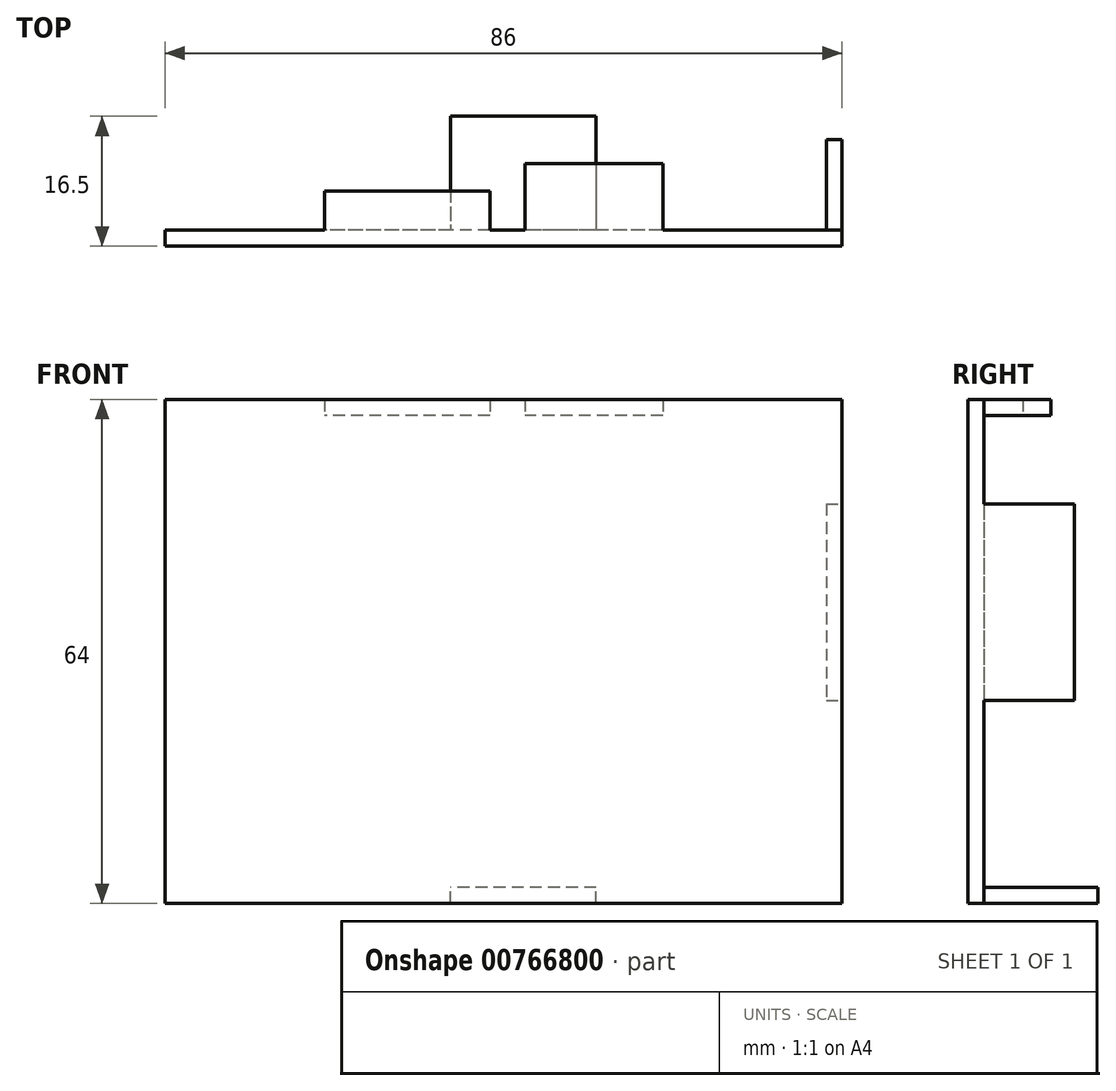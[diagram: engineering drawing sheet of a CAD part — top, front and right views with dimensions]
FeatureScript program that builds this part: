
annotation { "Feature Type Name" : "Feature", "Feature Type Description" : "" }
export const myFeature = defineFeature(function(context is Context, id is Id, definition is map)
    precondition{}
    {
        {
            var Q0;
            Q0=qCreatedBy(makeId("Front.planeOp"),FACE);
            var sketch = newSketch(context, id + "F0", { "sketchPlane" : qUnion([Q0])});
            skLineSegment(sketch, "E0.bottom", {"start": v(43, 32) * mm, "end": v(-43, 32) * mm});
            skLineSegment(sketch, "E0.top", {"start": v(43, -32) * mm, "end": v(-43, -32) * mm});
            skLineSegment(sketch, "E0.left", {"start": v(43, 32) * mm, "end": v(43, -32) * mm});
            skLineSegment(sketch, "E0.right", {"start": v(-43, 32) * mm, "end": v(-43, -32) * mm});
            skPoint(sketch, "E0.middle", {"position": v(0, 0) * mm});
            skLineSegment(sketch, "E1.bottom", {"start": v(41, 30) * mm, "end": v(-41, 30) * mm});
            skLineSegment(sketch, "E1.top", {"start": v(41, -30) * mm, "end": v(-41, -30) * mm});
            skLineSegment(sketch, "E1.left", {"start": v(41, 30) * mm, "end": v(41, -30) * mm});
            skLineSegment(sketch, "E1.right", {"start": v(-41, 30) * mm, "end": v(-41, -30) * mm});
            skLineSegment(sketch, "E2.bottom", {"start": v(-22.75, 32) * mm, "end": v(-1.75, 32) * mm});
            skLineSegment(sketch, "E2.top", {"start": v(-22.75, 30) * mm, "end": v(-1.75, 30) * mm});
            skLineSegment(sketch, "E2.left", {"start": v(-22.75, 32) * mm, "end": v(-22.75, 30) * mm});
            skLineSegment(sketch, "E2.right", {"start": v(-1.75, 32) * mm, "end": v(-1.75, 30) * mm});
            skLineSegment(sketch, "E3.bottom", {"start": v(2.75, 32) * mm, "end": v(20.25, 32) * mm});
            skLineSegment(sketch, "E3.top", {"start": v(2.75, 30) * mm, "end": v(20.25, 30) * mm});
            skLineSegment(sketch, "E3.left", {"start": v(2.75, 32) * mm, "end": v(2.75, 30) * mm});
            skLineSegment(sketch, "E3.right", {"start": v(20.25, 32) * mm, "end": v(20.25, 30) * mm});
            skLineSegment(sketch, "E4.bottom", {"start": v(-6.75, -32) * mm, "end": v(11.75, -32) * mm});
            skLineSegment(sketch, "E4.top", {"start": v(-6.75, -30) * mm, "end": v(11.75, -30) * mm});
            skLineSegment(sketch, "E4.left", {"start": v(-6.75, -32) * mm, "end": v(-6.75, -30) * mm});
            skLineSegment(sketch, "E4.right", {"start": v(11.75, -32) * mm, "end": v(11.75, -30) * mm});
            skLineSegment(sketch, "E5.bottom", {"start": v(41, 18.75) * mm, "end": v(43, 18.75) * mm});
            skLineSegment(sketch, "E5.top", {"start": v(41, -6.25) * mm, "end": v(43, -6.25) * mm});
            skLineSegment(sketch, "E5.left", {"start": v(41, 18.75) * mm, "end": v(41, -6.25) * mm});
            skLineSegment(sketch, "E5.right", {"start": v(43, 18.75) * mm, "end": v(43, -6.25) * mm});
            skSolve(sketch);
        }
        {
            var Q0;
            {var subQ2=sQuery(id+"F0.wireOp",EDGE,"E2.left");var subQ4=sQuery(id+"F0.wireOp",EDGE,"E0.right");var subQ5=sQuery(id+"F0.wireOp",EDGE,"E4.left");var subQ10=makeQuery(id+"F0.imprint","IMPRINT",EDGE,{"derivedFrom":subQ2});var subQ13=makeQuery(id+"F0.imprint","IMPRINT",EDGE,{"derivedFrom":subQ5});var subQ14=sQuery(id+"F0.wireOp",EDGE,"E2.right");var subQ17=makeQuery(id+"F0.imprint","IMPRINT",EDGE,{"derivedFrom":subQ14});var subQ18=sQuery(id+"F0.wireOp",EDGE,"E4.right");var subQ22=makeQuery(id+"F0.imprint","IMPRINT",EDGE,{"derivedFrom":subQ18});var subQ30=sQuery(id+"F0.wireOp",EDGE,"E5.bottom");var subQ33=makeQuery(id+"F0.imprint","IMPRINT",EDGE,{"derivedFrom":subQ30});var subQ34=sQuery(id+"F0.wireOp",EDGE,"E3.left");var subQ37=makeQuery(id+"F0.imprint","IMPRINT",EDGE,{"derivedFrom":subQ34});var subQ40=sQuery(id+"F0.wireOp",EDGE,"E3.right");var subQ43=makeQuery(id+"F0.imprint","IMPRINT",EDGE,{"derivedFrom":subQ40});Q0=qUnion([makeQuery(id+"F0.imprint","IMPRINT",FACE,{"disambiguationData":[TD([[subQ37,1.0]])]}),makeQuery(id+"F0.imprint","IMPRINT",FACE,{"disambiguationData":[TD([[subQ13,-1.0]])]}),makeQuery(id+"F0.imprint","IMPRINT",FACE,{"disambiguationData":[TD([[subQ43,1.0]])]}),makeQuery(id+"F0.imprint","IMPRINT",FACE,{"disambiguationData":[TD([[subQ17,1.0]])]}),makeQuery(id+"F0.imprint","IMPRINT",FACE,{"disambiguationData":[TD([[subQ33,-1.0]])]}),makeQuery(id+"F0.imprint","IMPRINT",FACE,{"disambiguationData":[TD([[subQ22,-1.0]])]}),makeQuery(id+"F0.imprint","IMPRINT",FACE,{"disambiguationData":[TD([[subQ10,1.0]])]}),makeQuery(id+"F0.imprint","IMPRINT",FACE,{"disambiguationData":[TD([[makeQuery(id+"F0.imprint","IMPRINT",EDGE,{"derivedFrom":subQ4}),1.0]])]})]);}
            var Q1;
            {var subQ7=sQuery(id+"F0.wireOp",EDGE,"E1.right");Q1=makeQuery(id+"F0.imprint","IMPRINT",FACE,{"disambiguationData":[TD([[makeQuery(id+"F0.imprint","IMPRINT",EDGE,{"derivedFrom":subQ7}),1.0]])]});}
            extrude(context, id + "F1", {"entities" : qUnion([Q0, Q1]), "depth" : 2 * mm, "offsetDistance" : 25 * mm});
        }
        {
            var Q0;
            {var subQ0=sQuery(id+"F0.wireOp",EDGE,"E4.left");Q0=makeQuery(id+"F0.imprint","IMPRINT",FACE,{"disambiguationData":[TD([[makeQuery(id+"F0.imprint","IMPRINT",EDGE,{"derivedFrom":subQ0}),-1.0]])]});}
            extrude(context, id + "F2", {"entities" : qUnion([Q0]), "operationType" : NewBodyOperationType.ADD, "oppositeDirection" : true, "depth" : 14.5 * mm, "offsetDistance" : 25 * mm});
        }
        {
            var Q0;
            {var subQ2=sQuery(id+"F0.wireOp",EDGE,"E5.bottom");Q0=makeQuery(id+"F0.imprint","IMPRINT",FACE,{"disambiguationData":[TD([[makeQuery(id+"F0.imprint","IMPRINT",EDGE,{"derivedFrom":subQ2}),-1.0]])]});}
            extrude(context, id + "F3", {"entities" : qUnion([Q0]), "operationType" : NewBodyOperationType.ADD, "oppositeDirection" : true, "depth" : 11.5 * mm, "offsetDistance" : 25 * mm});
        }
        {
            var Q0;
            {var subQ0=sQuery(id+"F0.wireOp",EDGE,"E3.left");Q0=makeQuery(id+"F0.imprint","IMPRINT",FACE,{"disambiguationData":[TD([[makeQuery(id+"F0.imprint","IMPRINT",EDGE,{"derivedFrom":subQ0}),1.0]])]});}
            extrude(context, id + "F4", {"entities" : qUnion([Q0]), "operationType" : NewBodyOperationType.ADD, "oppositeDirection" : true, "depth" : 8.5 * mm, "offsetDistance" : 25 * mm});
        }
        {
            var Q0;
            {var subQ2=sQuery(id+"F0.wireOp",EDGE,"E2.left");Q0=makeQuery(id+"F0.imprint","IMPRINT",FACE,{"disambiguationData":[TD([[makeQuery(id+"F0.imprint","IMPRINT",EDGE,{"derivedFrom":subQ2}),1.0]])]});}
            extrude(context, id + "F5", {"entities" : qUnion([Q0]), "operationType" : NewBodyOperationType.ADD, "oppositeDirection" : true, "depth" : 5 * mm, "offsetDistance" : 25 * mm});
        }
    });
